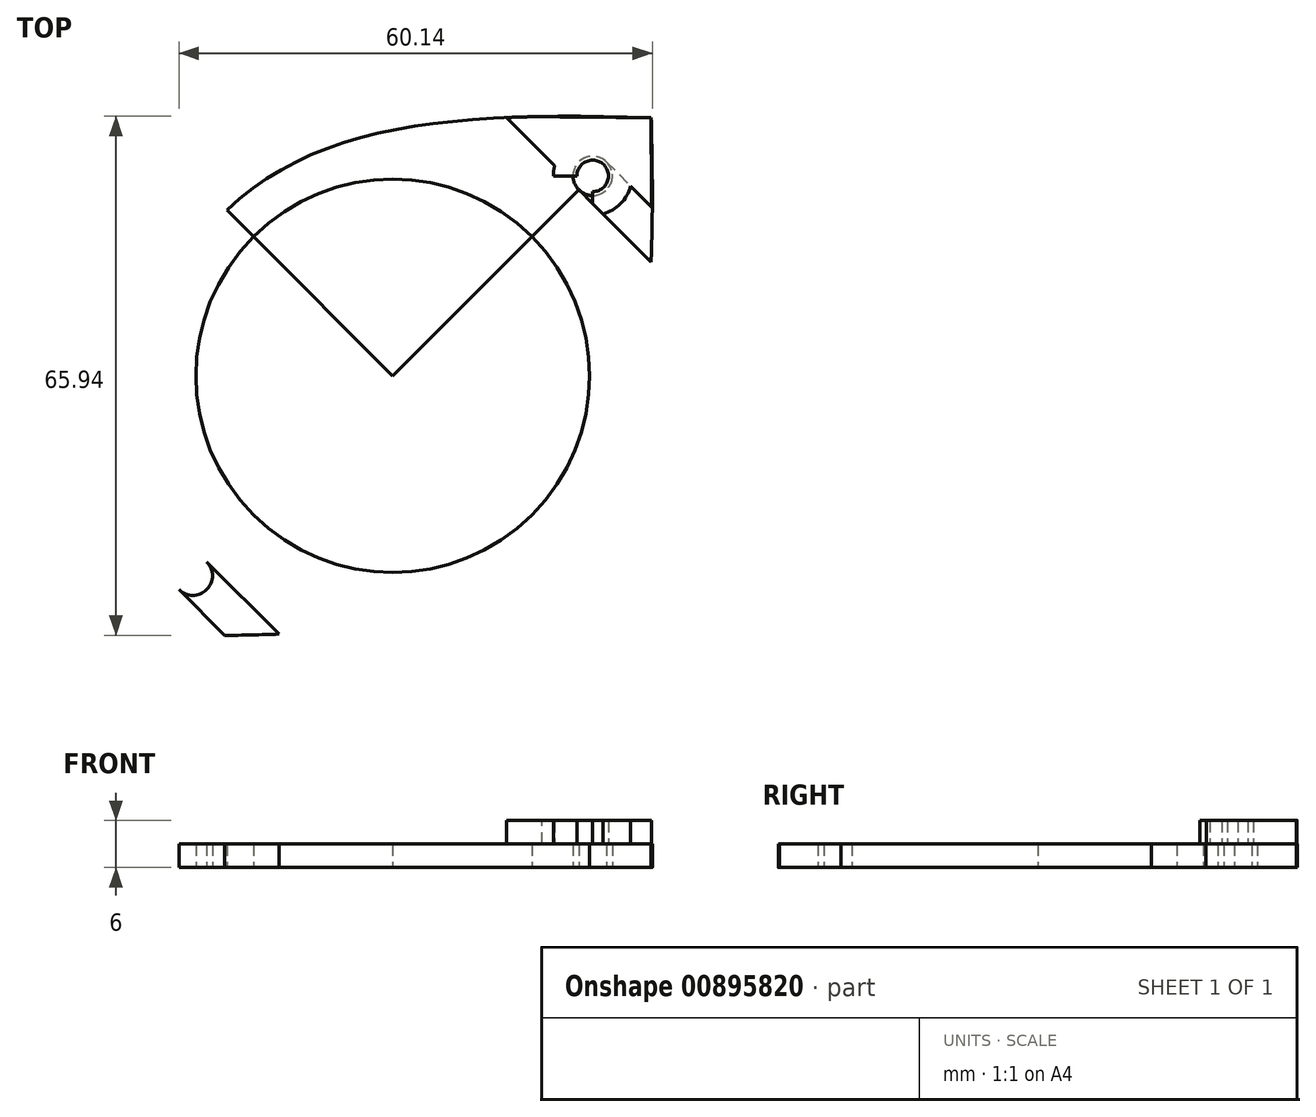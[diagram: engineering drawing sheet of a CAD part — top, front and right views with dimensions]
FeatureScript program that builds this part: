
annotation { "Feature Type Name" : "Feature", "Feature Type Description" : "" }
export const myFeature = defineFeature(function(context is Context, id is Id, definition is map)
    precondition{}
    {
        {
            var Q0;
            Q0=qCreatedBy(makeId("Top.planeOp"),FACE);
            var sketch = newSketch(context, id + "F0", { "sketchPlane" : qUnion([Q0])});
            skFitSpline(sketch, "E0", {"points": [v(-24.7, 17.03) * mm, v(32.82, 32.82) * mm], "startDerivative": vector(36.15, 46.2) * mm, "endDerivative": vector(78.55, -2.04) * mm});
            skArc(sketch, "E1", {"start": v(17.68, 17.68) * mm, "mid": v(0, 25) * mm, "end": v(-17.68, 17.68) * mm});
            skLineSegment(sketch, "E2", {"start": v(0, 0) * mm, "end": v(66.67, 66.67) * mm});
            skLineSegment(sketch, "E3", {"start": v(0, 0) * mm, "end": v(-37.06, 37.06) * mm});
            skFitSpline(sketch, "E4.MirrorCS", {"points": [v(17.03, -24.7) * mm, v(32.82, 32.82) * mm], "startDerivative": vector(46.2, 36.15) * mm, "endDerivative": vector(-2.04, 78.55) * mm});
            skArc(sketch, "E5.MirrorCS", {"start": v(17.68, 17.68) * mm, "mid": v(25, 0) * mm, "end": v(17.68, -17.68) * mm});
            skArc(sketch, "E6.MirrorCS", {"start": v(-17.68, -17.68) * mm, "mid": v(-25, 0) * mm, "end": v(-17.68, 17.68) * mm});
            skArc(sketch, "E7.MirrorCS", {"start": v(-17.68, -17.68) * mm, "mid": v(0, -25) * mm, "end": v(17.68, -17.68) * mm});
            skFitSpline(sketch, "E8.MirrorCS", {"points": [v(24.7, -17.03) * mm, v(-32.82, -32.82) * mm], "startDerivative": vector(-36.15, -46.2) * mm, "endDerivative": vector(-78.55, 2.04) * mm});
            skFitSpline(sketch, "E9.MirrorCS", {"points": [v(-17.03, 24.7) * mm, v(-32.82, -32.82) * mm], "startDerivative": vector(-46.2, -36.15) * mm, "endDerivative": vector(2.04, -78.55) * mm});
            skCircle(sketch, "E10", {"center": v(25.4, 25.4) * mm, "radius": 2.5 * mm});
            skLineSegment(sketch, "E11", {"start": v(27.17, 27.17) * mm, "end": v(32.97, 21.37) * mm});
            skLineSegment(sketch, "E12", {"start": v(23.63, 23.63) * mm, "end": v(32.8, 14.46) * mm});
            skCircle(sketch, "E13.MirrorC", {"center": v(-25.4, -25.4) * mm, "radius": 2.5 * mm});
            skLineSegment(sketch, "E14.MirrorCS", {"start": v(-27.17, -27.17) * mm, "end": v(-21.37, -32.97) * mm});
            skLineSegment(sketch, "E15.MirrorCS", {"start": v(-23.63, -23.63) * mm, "end": v(-14.46, -32.8) * mm});
            skSolve(sketch);
        }
        {
            var Q0;
            {var subQ8=sQuery(id+"F0.wireOp",EDGE,"E5.MirrorCS");Q0=makeQuery(id+"F0.imprint","IMPRINT",FACE,{"disambiguationData":[TD([[makeQuery(id+"F0.imprint","IMPRINT",EDGE,{"derivedFrom":subQ8}),1.0]])]});}
            var Q1;
            {var subQ4=sQuery(id+"F0.wireOp",EDGE,"E0");Q1=makeQuery(id+"F0.imprint","IMPRINT",FACE,{"disambiguationData":[TD([[makeQuery(id+"F0.imprint","IMPRINT",EDGE,{"derivedFrom":subQ4}),-1.0]])]});}
            var Q2;
            {var subQ3=sQuery(id+"F0.wireOp",EDGE,"E11");Q2=makeQuery(id+"F0.imprint","IMPRINT",FACE,{"disambiguationData":[TD([[makeQuery(id+"F0.imprint","IMPRINT",EDGE,{"derivedFrom":subQ3}),1.0]])]});}
            extrude(context, id + "F1", {"entities" : qUnion([Q0, Q1, Q2]), "depth" : 3 * mm, "offsetDistance" : 25 * mm});
        }
        {
            var Q0;
            {var subQ0=sQuery(id+"F0.wireOp",EDGE,"E11");Q0=makeQuery(id+"F0.imprint","IMPRINT",FACE,{"disambiguationData":[TD([[makeQuery(id+"F0.imprint","IMPRINT",EDGE,{"derivedFrom":subQ0}),-1.0]])]});}
            var Q1;
            {var subQ0=sQuery(id+"F0.wireOp",EDGE,"E14.MirrorCS");Q1=makeQuery(id+"F0.imprint","IMPRINT",FACE,{"disambiguationData":[TD([[makeQuery(id+"F0.imprint","IMPRINT",EDGE,{"derivedFrom":subQ0}),1.0]])]});}
            extrude(context, id + "F2", {"entities" : qUnion([Q0, Q1]), "depth" : 3 * mm, "offsetDistance" : 25 * mm});
        }
        {
            var Q0;
            Q0=makeQuery(id+"F1.opExtrude","CAP_FACE",FACE,{"disambiguationData":[OSD([sQuery(id+"F0.wireOp",EDGE,"E0"),sQuery(id+"F0.wireOp",EDGE,"E1"),sQuery(id+"F0.wireOp",EDGE,"E4.MirrorCS"),sQuery(id+"F0.wireOp",EDGE,"E5.MirrorCS"),sQuery(id+"F0.wireOp",EDGE,"E6.MirrorCS"),sQuery(id+"F0.wireOp",EDGE,"E7.MirrorCS"),sQuery(id+"F0.wireOp",EDGE,"E8.MirrorCS"),sQuery(id+"F0.wireOp",EDGE,"E9.MirrorCS"),sQuery(id+"F0.wireOp",EDGE,"E10"),sQuery(id+"F0.wireOp",EDGE,"E11"),sQuery(id+"F0.wireOp",EDGE,"E12"),sQuery(id+"F0.wireOp",EDGE,"E13.MirrorC"),sQuery(id+"F0.wireOp",EDGE,"E14.MirrorCS"),sQuery(id+"F0.wireOp",EDGE,"E15.MirrorCS")])],"isStart":false});
            var sketch = newSketch(context, id + "F3", { "sketchPlane" : qUnion([Q0])});
            skCircle(sketch, "E16", {"center": v(25.4, 25.4) * mm, "radius": 5 * mm});
            skCircle(sketch, "E17", {"center": v(25.4, 25.4) * mm, "radius": 2 * mm});
            skLineSegment(sketch, "E18", {"start": v(25.4, 25.4) * mm, "end": v(25.4, 20.4) * mm});
            skLineSegment(sketch, "E19", {"start": v(25.4, 25.4) * mm, "end": v(20.4, 25.4) * mm});
            skLineSegment(sketch, "E20.0", {"start": v(23.63, 23.63) * mm, "end": v(32.8, 14.46) * mm});
            skLineSegment(sketch, "E20.1", {"start": v(27.17, 27.17) * mm, "end": v(32.97, 21.37) * mm});
            skFitSpline(sketch, "E20.2", {"points": [v(17.03, -24.7) * mm, v(32.43, -12.65) * mm, v(33.5, 6.64) * mm, v(32.82, 32.82) * mm]});
            skLineSegment(sketch, "E21.MirrorCS", {"start": v(27.17, 27.17) * mm, "end": v(21.37, 32.97) * mm});
            skLineSegment(sketch, "E22.MirrorCS", {"start": v(23.63, 23.63) * mm, "end": v(14.46, 32.8) * mm});
            skFitSpline(sketch, "E23.MirrorCS", {"points": [v(-24.7, 17.03) * mm, v(-12.65, 32.43) * mm, v(6.64, 33.5) * mm, v(32.82, 32.82) * mm]});
            skSolve(sketch);
        }
        {
            var Q0;
            {var subQ0=sQuery(id+"F3.wireOp",EDGE,"E19");var subQ1=sQuery(id+"F3.wireOp",EDGE,"E16");var subQ2=makeQuery(id+"F3.imprint","INTERSECT",VERTEX,{"derivedFrom":[subQ1,subQ0]});Q0=makeQuery(id+"F3.imprint","IMPRINT",FACE,{"disambiguationData":[TD([[makeQuery(id+"F3.imprint","IMPRINT",EDGE,{"disambiguationData":[TD([[subQ2,1.0]])],"derivedFrom":subQ1}),1.0]])]});}
            var Q1;
            {var subQ7=sQuery(id+"F3.wireOp",EDGE,"E20.0");var subQ9=sQuery(id+"F3.wireOp",EDGE,"E16");var subQ10=makeQuery(id+"F3.imprint","INTERSECT",VERTEX,{"derivedFrom":[subQ9,subQ7]});Q1=makeQuery(id+"F3.imprint","IMPRINT",FACE,{"disambiguationData":[TD([[makeQuery(id+"F3.imprint","IMPRINT",EDGE,{"disambiguationData":[TD([[subQ10,-1.0]])],"derivedFrom":subQ9}),1.0]])]});}
            var Q2;
            {var subQ5=sQuery(id+"F3.wireOp",EDGE,"E20.2");Q2=makeQuery(id+"F3.imprint","IMPRINT",FACE,{"disambiguationData":[TD([[makeQuery(id+"F3.imprint","IMPRINT",EDGE,{"derivedFrom":subQ5}),1.0]])]});}
            var Q3;
            {var subQ5=sQuery(id+"F3.wireOp",EDGE,"E23.MirrorCS");Q3=makeQuery(id+"F3.imprint","IMPRINT",FACE,{"disambiguationData":[TD([[makeQuery(id+"F3.imprint","IMPRINT",EDGE,{"derivedFrom":subQ5}),-1.0]])]});}
            var Q4;
            {var subQ0=sQuery(id+"F3.wireOp",EDGE,"E22.MirrorCS");var subQ1=sQuery(id+"F3.wireOp",EDGE,"E16");var subQ2=makeQuery(id+"F3.imprint","INTERSECT",VERTEX,{"derivedFrom":[subQ1,subQ0]});Q4=makeQuery(id+"F3.imprint","IMPRINT",FACE,{"disambiguationData":[TD([[makeQuery(id+"F3.imprint","IMPRINT",EDGE,{"disambiguationData":[TD([[subQ2,1.0]])],"derivedFrom":subQ1}),1.0]])]});}
            var Q5;
            {var subQ0=sQuery(id+"F3.wireOp",EDGE,"E21.MirrorCS");var subQ1=sQuery(id+"F3.wireOp",EDGE,"E16");var subQ2=makeQuery(id+"F3.imprint","INTERSECT",VERTEX,{"derivedFrom":[subQ1,subQ0]});Q5=makeQuery(id+"F3.imprint","IMPRINT",FACE,{"disambiguationData":[TD([[makeQuery(id+"F3.imprint","IMPRINT",EDGE,{"disambiguationData":[TD([[subQ2,1.0]])],"derivedFrom":subQ1}),1.0]])]});}
            extrude(context, id + "F4", {"entities" : qUnion([Q0, Q1, Q2, Q3, Q4, Q5]), "depth" : 3 * mm, "offsetDistance" : 25 * mm});
        }
    });
